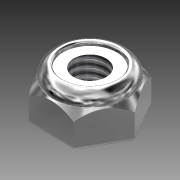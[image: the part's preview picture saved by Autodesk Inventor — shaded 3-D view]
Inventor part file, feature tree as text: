
AUTODESK INVENTOR PART (.ipt)
format: ipt  version: 2012 (Build 160160000, 160)  size: 154,624 bytes
history: native  units: in
note: dims shown in document units (in); Inventor stores cm internally (conversion verified against a paired STEP export)
features: other x1, imported_body x1, thread x1
ambient origin geometry x8: Origin, YZ Plane, XZ Plane, XY Plane, X Axis, Y Axis, Z Axis, Center Point
feature tree (3):
  parser-record x1  (decoder bookkeeping rows leaked as tree rows — omitted from the tree; the rows remain in map.json)
  imported_body  "Base1"
  thread  "Thread1"  [1 undecoded]
note: 1 required parameter value undecoded (feature->parameter linkage not recoverable at this tier; creation-order binding heuristic only, values carry confidence <= 0.55)
